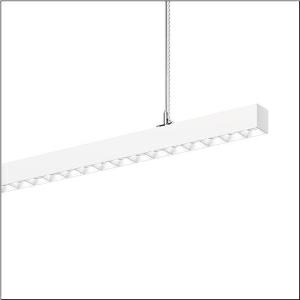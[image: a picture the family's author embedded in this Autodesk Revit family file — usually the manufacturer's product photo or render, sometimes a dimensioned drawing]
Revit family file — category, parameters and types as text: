
# Revit family: silica_r__21_51mx36dc3dwb_b05b
name_source: partatom
category: Lighting Fixtures
units: mm (PartAtom-declared; Revit-internal decimal feet)

## family parameters
Cut with Voids When Loaded = No
Host = Face
Light Source = No
Part Type = Normal
Room Calculation Point = No
Round Connector Dimension = Use Diameter
Shared = No

## types (1)
- --- (1 x LED, 17650 lm, 104.1 W, 3000K)
    Apparent Load = 104 VA
    CIE Flux Codes = 83 98 100 61 100
    Color Rendering = 80
    Color Temperature = 3000K
    Default Elevation = 1800 mm
    Description = Silica® 21, office luminaire, primary light control with darklight reflector, of PMMA, white, CAT 2 (L<= 3000cd/m²), light emission: direct/indirect distribution, primary light characteristic: symmetric, installation type: suspended mounting, LED, rated luminous flux: 17.650lm, luminous efficacy: 170lm/W, light colour: 830, colour temperature: 3000K, with terminal, 3+2-pole, max. 2.5mm², mains connection: 220..240V, AC, 50/60Hz, rated input power: 104.1W, luminaire housing, of aluminium, traffic white (RAL 9016), length: 3.004mm, width: 53mm, height: 53mm, protection rating (complete): IP20, insulation class (complete): insulation class I (protective earthing), certification: CE, permissible operating ambient temperature: 0..+35°C, standard: EN 50419, packaging unit: 1 piece
    Height = 53 mm
    Lamp = 1 x LED
    Lamp Light Flux = 17650 lm
    Lamp Power = 104.1 W
    Lamp count = 1
    Length = 3004 mm
    Luminous efficacy = 170 lm/W
    Manufacturer = Siteco
    ModVariant = No
    Model = 51MX36DC3DWB
    Mounting Place = Ceiling
    Mounting Type = Pendant
    Number of Poles = 1
    OnlyDefault = Yes
    Power Factor = 1
    Product Name = Silica® 21
    Product group = office luminaire | ceiling pendant
    ProductGroupID = 902
    Protection Class = Protection class I
    Protection Degree = IP 20
    RLX_Detail_Level = 1
    RLX_Emergency_Light_Flux = 0 lm
    RLX_Emergency_Type = 0
    RLX_Emergency_Type_DB = No
    RlxData = <blob elided: 63253 chars, md5=fbfa0ee4>
    Socket = socket
    Standby Power = 0 W
    System Light Flux = 17650 lm
    System Power = 104 W
    Type Comments = factory setting: luminous flux: 100 % | dim-lin: 254 | 359 mA
    Type Image = l_1335921.jpg
    URL = http://relux.com
    VarID = @adj_090941
    Voltage = 0 V
    Weight = 0.00 kg
    Width = 53 mm

## geometry (parser evidence)
native form markers: Blend x4, Sweep x15
no freeform markers — native parametric forms only
